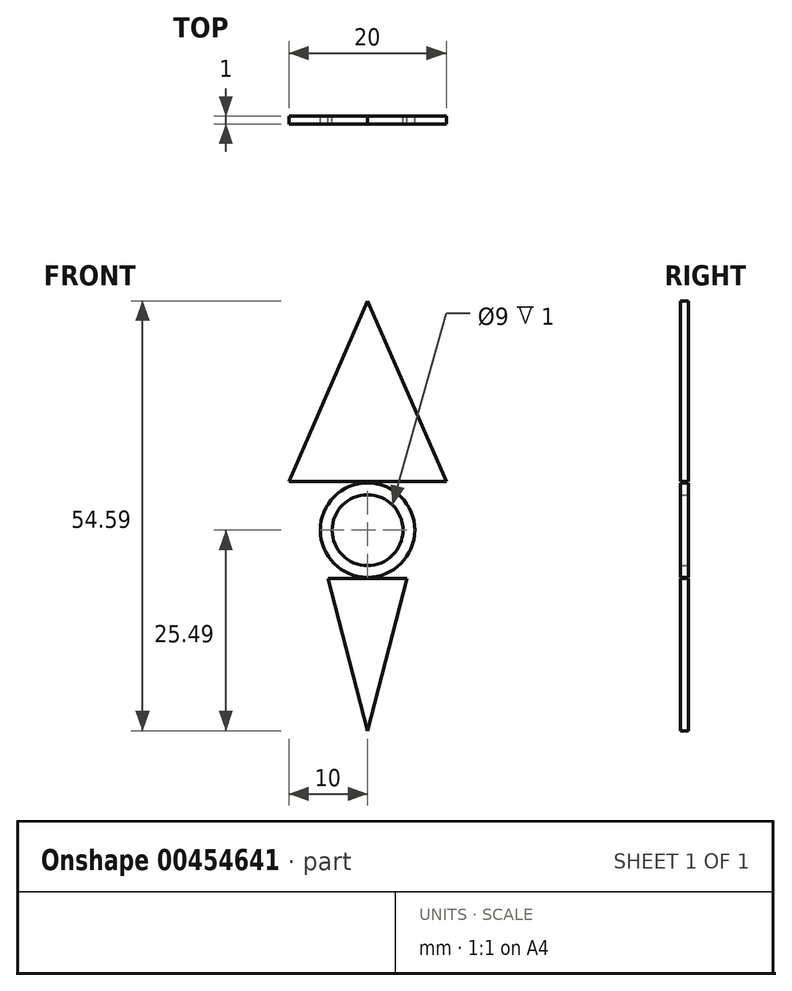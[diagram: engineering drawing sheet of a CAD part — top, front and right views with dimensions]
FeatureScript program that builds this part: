
annotation { "Feature Type Name" : "Feature", "Feature Type Description" : "" }
export const myFeature = defineFeature(function(context is Context, id is Id, definition is map)
    precondition{}
    {
        {
            var Q0;
            Q0=qCreatedBy(makeId("Front.planeOp"),FACE);
            var sketch = newSketch(context, id + "F0", { "sketchPlane" : qUnion([Q0])});
            skCircle(sketch, "E0", {"center": v(0, 0) * mm, "radius": 4.5 * mm});
            skCircle(sketch, "E1", {"center": v(0, 0) * mm, "radius": 6 * mm});
            skLineSegment(sketch, "E2", {"start": v(-5, -6.12) * mm, "end": v(5, -6.12) * mm});
            skLineSegment(sketch, "E3", {"start": v(5, -6.12) * mm, "end": v(0, -25.49) * mm});
            skLineSegment(sketch, "E4", {"start": v(0, -25.49) * mm, "end": v(-5, -6.12) * mm});
            skLineSegment(sketch, "E5", {"start": v(-10, 6.2) * mm, "end": v(10, 6.2) * mm});
            skLineSegment(sketch, "E6", {"start": v(10, 6.2) * mm, "end": v(0, 29.1) * mm});
            skLineSegment(sketch, "E7", {"start": v(0, 29.1) * mm, "end": v(-10, 6.2) * mm});
            skSolve(sketch);
        }
        {
            var Q0;
            Q0 = qSketchRegion(id + "F0", true);
            extrude(context, id + "F1", {"entities" : qUnion([Q0]), "depth" : 1 * mm, "offsetDistance" : 25 * mm});
        }
    });
